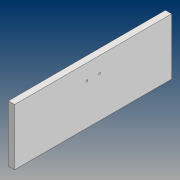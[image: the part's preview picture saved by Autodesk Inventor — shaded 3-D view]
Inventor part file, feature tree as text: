
AUTODESK INVENTOR PART (.ipt)
format: ipt  version: 2021 (Build 250183000, 183)  size: 91,136 bytes
history: native  units: mm
features: sketch x2, extrude x1, hole x1, projected_geometry x1
ambient origin geometry x8: Origin, YZ Plane, XZ Plane, XY Plane, X Axis, Y Axis, Z Axis, Center Point
bodies: Solid1 (feature_tree)
feature tree (5):
  extrude  "Extrusion1"  Depth=90.0mm
  hole  "Hole1"  [1 undecoded]
  sketch  "Sketch1"  dims[d0=250.0mm d1=90.0mm]
  sketch  "Sketch2"  dims[d2=10.0mm d3=0.0mm d4=20.0mm d5=25.0mm d6=3.2mm d7=6.0mm d8=4.0mm d9=2.0mm d10=90.0deg d11=8.0mm d12=20.594885mm]
  projected_geometry  "Projected Loop1"
note: 1 required parameter value undecoded (feature->parameter linkage not recoverable at this tier; creation-order binding heuristic only, values carry confidence <= 0.55)
